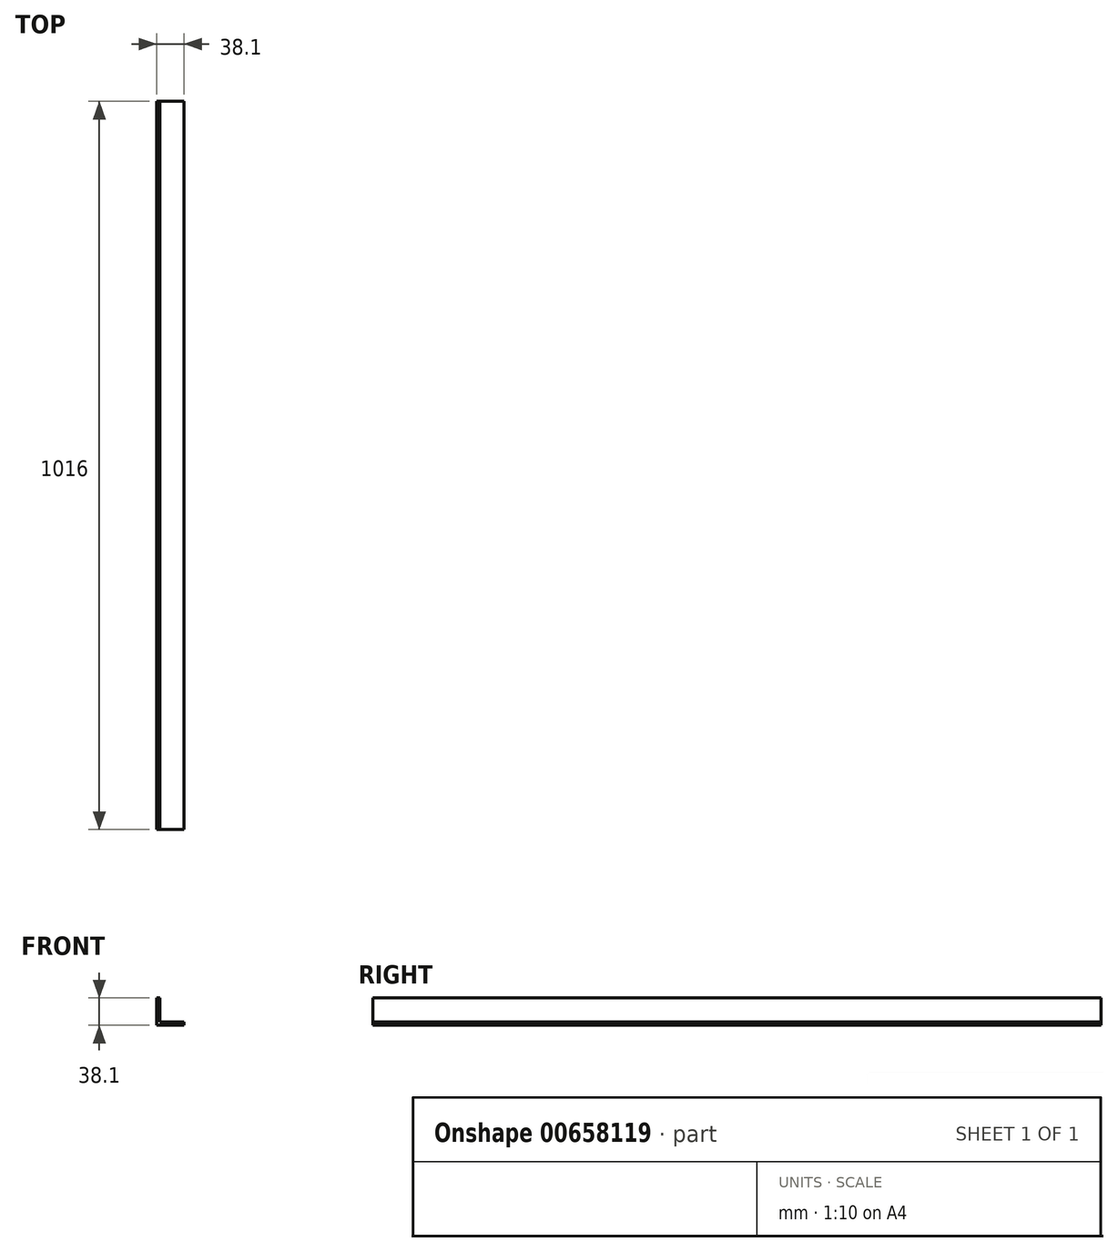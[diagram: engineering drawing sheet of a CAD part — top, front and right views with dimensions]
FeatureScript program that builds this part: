
annotation { "Feature Type Name" : "Feature", "Feature Type Description" : "" }
export const myFeature = defineFeature(function(context is Context, id is Id, definition is map)
    precondition{}
    {
        {
            var Q0;
            Q0=qCreatedBy(makeId("Front.planeOp"),FACE);
            var sketch = newSketch(context, id + "F0", { "sketchPlane" : qUnion([Q0])});
            skLineSegment(sketch, "E0", {"start": v(0, 0) * mm, "end": v(0, 38.1) * mm});
            skLineSegment(sketch, "E1", {"start": v(0, 38.1) * mm, "end": v(4.76, 38.1) * mm});
            skLineSegment(sketch, "E2", {"start": v(4.76, 38.1) * mm, "end": v(4.76, 4.76) * mm});
            skLineSegment(sketch, "E3", {"start": v(4.76, 4.76) * mm, "end": v(38.1, 4.76) * mm});
            skLineSegment(sketch, "E4", {"start": v(38.1, 4.76) * mm, "end": v(38.1, 0) * mm});
            skLineSegment(sketch, "E5", {"start": v(38.1, 0) * mm, "end": v(0, 0) * mm});
            skSolve(sketch);
        }
        {
            var Q0;
            Q0=qSketchRegion(id+"F0",true);
            extrude(context, id + "F1", {"entities" : qUnion([Q0]), "oppositeDirection" : true, "depth" : 1016 * mm, "offsetDistance" : 25.4 * mm});
        }
    });
